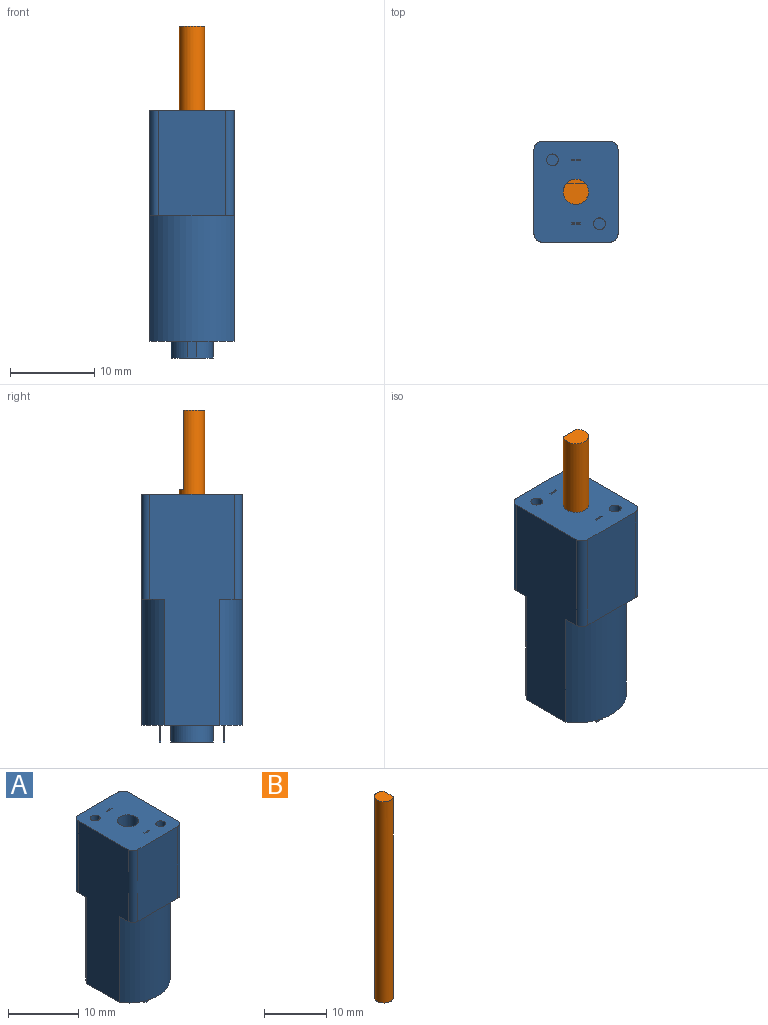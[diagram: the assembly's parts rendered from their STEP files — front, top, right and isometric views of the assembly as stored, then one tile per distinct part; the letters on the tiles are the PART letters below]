
ASSEMBLY  parts=2 mates=1
PART A: 43 faces, bbox 10x12x29.5 mm
  f0: plane 5x2.68mm, normal (0,0,-1), area 3.8mm2, adj f9,f15,f20,f26
  f1: plane 5x2.68mm, normal (0,0,-1), area 3.8mm2, adj f9,f10,f11,f26
  f2: plane 5x2.68mm, normal (0,0,-1), area 3.8mm2, adj f11,f12,f13,f25
  f3: plane 12.5x1mm, normal (0,-1,0), area 12.5mm2, adj f4,f18,f22,f36
  f4: plane 12.5x0.2mm, normal (-1,0,0), area 2.5mm2, adj f3,f5,f22,f36
  f5: plane 12.5x1mm, normal (0,1,0), area 12.5mm2, adj f4,f18,f22,f36
  f6: plane 12.5x0.2mm, normal (-1,0,0), area 2.5mm2, adj f7,f19,f22,f42
  f7: plane 12.5x1mm, normal (0,1,0), area 12.5mm2, adj f6,f8,f22,f42
  f8: plane 12.5x0.2mm, normal (1,0,0), area 2.5mm2, adj f7,f19,f22,f42
  f9: plane 12.5x8mm, normal (0,-1,0), area 100mm2, adj f0,f1,f10,f20,f22
  f10: cylinder r=1mm len=12.5mm, axis (0,0,-1), area 19.6mm2, adj f1,f9,f11,f22
  f11: plane 27.5x10mm, normal (1,0,0), area 224.5mm2, adj f1,f2,f10,f12,f22,f24,f25,f26
  f12: cylinder r=1mm len=12.5mm, axis (0,0,-1), area 19.6mm2, adj f2,f11,f13,f22
  f13: plane 12.5x8mm, normal (0,1,0), area 100mm2, adj f2,f12,f14,f22,f23
  f14: cylinder r=1mm len=12.5mm, axis (0,0,-1), area 19.6mm2, adj f13,f15,f22,f23
  f15: plane 27.5x10mm, normal (-1,0,0), area 224.5mm2, adj f0,f14,f20,f22,f23,f24,f25,f26
  f16: cylinder r=0.7mm len=12.5mm, axis (0,0,-1), area 55mm2, adj f22,f27
  f17: cylinder r=0.7mm len=12.5mm, axis (0,0,-1), area 55mm2, adj f22,f28
  f18: plane 12.5x0.2mm, normal (1,0,0), area 2.5mm2, adj f3,f5,f22,f36
  f19: plane 12.5x1mm, normal (0,-1,0), area 12.5mm2, adj f6,f8,f22,f42
  f20: cylinder r=1mm len=12.5mm, axis (0,0,-1), area 19.6mm2, adj f0,f9,f15,f22
  f21: cylinder r=1.5mm len=29.5mm, axis (0,0,-1), area 278mm2, adj f22,f30
  f22: plane 12x10mm, normal (0,0,1), area 108.6mm2, adj f3,f4,f5,f6,f7,f8,f9,f10
  f23: plane 5x2.68mm, normal (0,0,-1), area 3.8mm2, adj f13,f14,f15,f25
  f24: plane 12x10mm, normal (0,0,-1), area 84.1mm2, adj f11,f15,f25,f26,f29,f32,f33,f34
  f25: cylinder r=6mm len=15mm, axis (0,0,1), area 177.3mm2, adj f2,f11,f15,f23,f24
  f26: cylinder r=6mm len=15mm, axis (0,0,1), area 177.3mm2, adj f0,f1,f11,f15,f24
  f27: plane 1.4x1.4mm, normal (0,0,1), area 1.5mm2, adj f16
  f28: plane 1.4x1.4mm, normal (0,0,1), area 1.5mm2, adj f17
  f29: cylinder r=2.5mm len=5mm, axis (0,0,1), area 31.4mm2, adj f24,f30
  f30: plane 5x5mm, normal (0,0,-1), area 12.6mm2, adj f21,f29
  f31: plane 1x0.2mm, normal (0,0,-1), area 0.2mm2, adj f32,f33,f34,f35
  f32: plane 2x1mm, normal (0,1,0), area 2mm2, adj f24,f31,f33,f35
  f33: plane 2x0.2mm, normal (1,0,0), area 0.4mm2, adj f24,f31,f32,f34
  f34: plane 2x1mm, normal (0,-1,0), area 2mm2, adj f24,f31,f33,f35
  f35: plane 2x0.2mm, normal (-1,0,0), area 0.4mm2, adj f24,f31,f32,f34
  f36: plane 1x0.2mm, normal (0,0,1), area 0.2mm2, adj f3,f4,f5,f18
  f37: plane 1x0.2mm, normal (0,0,-1), area 0.2mm2, adj f38,f39,f40,f41
  f38: plane 2x1mm, normal (0,1,0), area 2mm2, adj f24,f37,f39,f41
  f39: plane 2x0.2mm, normal (1,0,0), area 0.4mm2, adj f24,f37,f38,f40
  f40: plane 2x1mm, normal (0,-1,0), area 2mm2, adj f24,f37,f39,f41
  f41: plane 2x0.2mm, normal (-1,0,0), area 0.4mm2, adj f24,f37,f38,f40
  f42: plane 1x0.2mm, normal (0,0,1), area 0.2mm2, adj f6,f7,f8,f19
PART B: 5 faces, bbox 3x3x39.5 mm
  f0: plane 9.5x2.24mm, normal (1,0,0), area 21.2mm2, adj f1,f2,f4
  f1: cylinder r=1.5mm len=39.5mm, axis (0,0,-1), area 348.3mm2, adj f0,f2,f3,f4
  f2: plane 3x2.5mm, normal (0,0,1), area 6.3mm2, adj f0,f1
  f3: plane 3x3mm, normal (0,0,-1), area 7.1mm2, adj f1
  f4: plane 2.24x0.5mm, normal (0,0,1), area 0.8mm2, adj f0,f1
PLACE A t=(-1.94,0.68,-0.41)mm fixed
PLACE B rot(axis=(0,0,1),89.6deg) t=(-1.94,0.68,-0.41)mm
MATE revolute A.f21 <-> B.f1  axis (0,0,-1) through (-1.94,0.68,-17.41)mm
